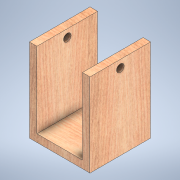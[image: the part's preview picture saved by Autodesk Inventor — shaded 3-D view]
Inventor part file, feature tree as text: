
AUTODESK INVENTOR PART (.ipt)
format: ipt  version: 2021 (Build 250183000, 183)  size: 152,064 bytes
history: native  units: in
note: dims shown in document units (in); Inventor stores cm internally (conversion verified against a paired STEP export)
features: extrude x3, sketch x3
ambient origin geometry x8: Origin, YZ Plane, XZ Plane, XY Plane, X Axis, Y Axis, Z Axis, Center Point
bodies: Solid1 (feature_tree)
feature tree (6):
  extrude  "Extrusion1"  Depth=8.0in
  extrude  "Extrusion2"  Depth=1.0in
  extrude  "Extrusion4"  Depth=10.0in TaperAngle=0.0deg
  sketch  "Sketch1"  dims[d0=8.0in d1=8.0in]
  sketch  "Sketch2"  dims[d2=1.0in d3=0.0in d4=1.0in]
  sketch  "Sketch3"  dims[d5=1.0in d6=10.0in d7=0.0in d8=1.0in d9=1.0in d12=0.0in d13=0.0in]
